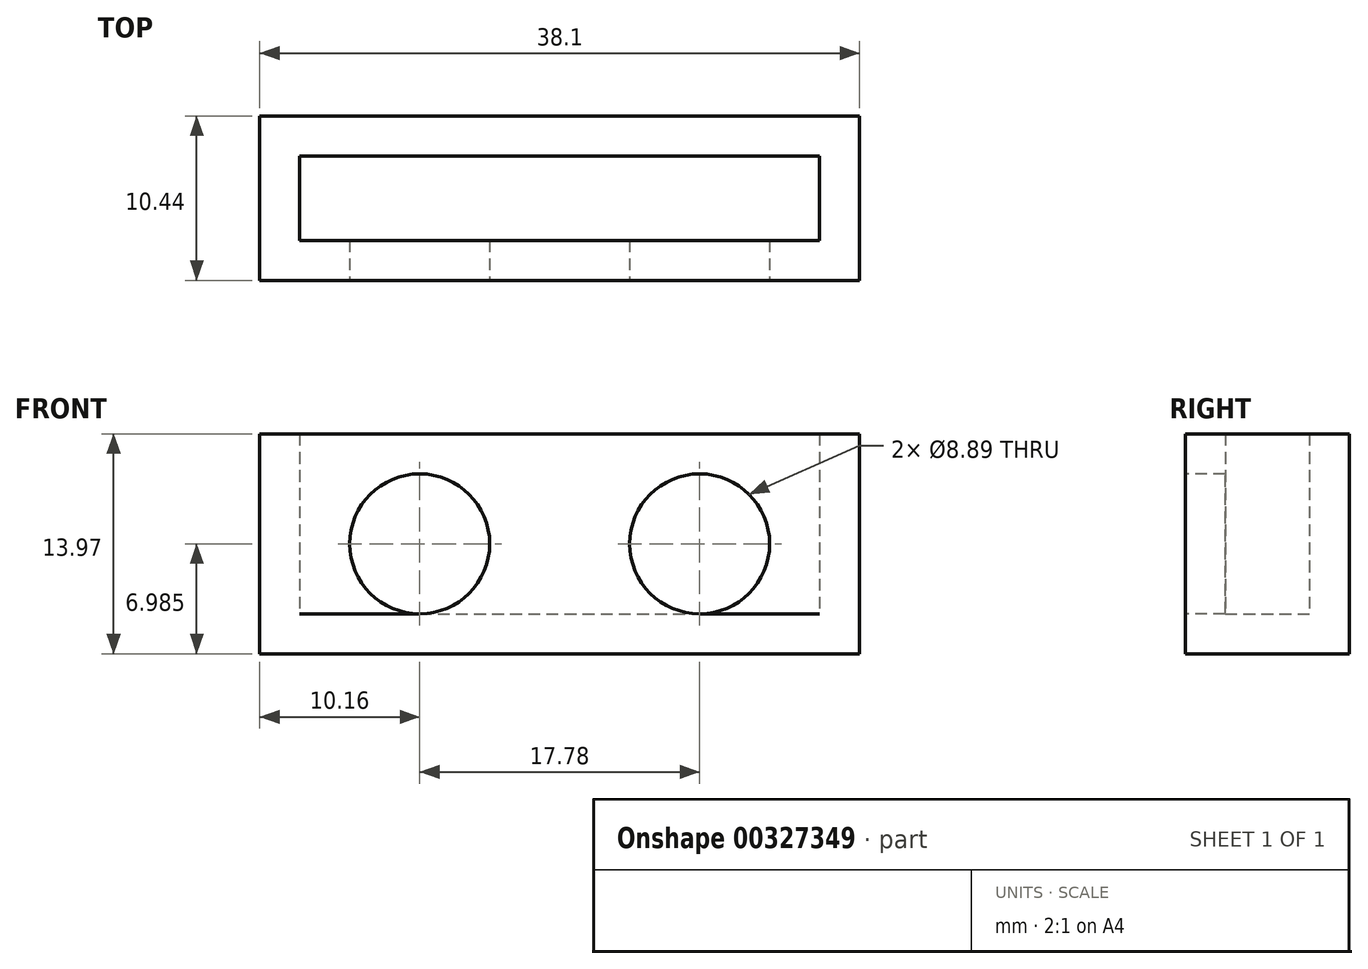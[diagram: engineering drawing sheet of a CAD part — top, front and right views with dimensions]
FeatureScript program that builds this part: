
annotation { "Feature Type Name" : "Feature", "Feature Type Description" : "" }
export const myFeature = defineFeature(function(context is Context, id is Id, definition is map)
    precondition{}
    {
        {
            var Q0;
            Q0=qCreatedBy(makeId("Top.planeOp"),FACE);
            var sketch = newSketch(context, id + "F0", { "sketchPlane" : qUnion([Q0])});
            skLineSegment(sketch, "E0.bottom", {"start": v(-19.05, -5.22) * mm, "end": v(19.05, -5.22) * mm});
            skLineSegment(sketch, "E0.top", {"start": v(-19.05, 5.22) * mm, "end": v(19.05, 5.22) * mm});
            skLineSegment(sketch, "E0.left", {"start": v(-19.05, -5.22) * mm, "end": v(-19.05, 5.22) * mm});
            skLineSegment(sketch, "E0.right", {"start": v(19.05, -5.22) * mm, "end": v(19.05, 5.22) * mm});
            skPoint(sketch, "E0.middle", {"position": v(0, 0) * mm});
            skSolve(sketch);
        }
        {
            var Q0;
            Q0 = qSketchRegion(id + "F0", true);
            extrude(context, id + "F1", {"entities" : qUnion([Q0]), "depth" : 13.97 * mm});
        }
        {
            var Q0;
            Q0=makeQuery(id+"F1.opExtrude","CAP_FACE",FACE,{"disambiguationData":[OSD([sQuery(id+"F0.wireOp",EDGE,"E0.bottom"),sQuery(id+"F0.wireOp",EDGE,"E0.top"),sQuery(id+"F0.wireOp",EDGE,"E0.left"),sQuery(id+"F0.wireOp",EDGE,"E0.right")])],"isStart":false});
            shell(context, id + "F2", {"entities" : qUnion([Q0]), "thickness" : 2.54 * mm});
        }
        {
            var Q0;
            Q0=makeQuery(id+"F1.opExtrude","SWEPT_FACE",FACE,{"disambiguationData":[OSD([sQuery(id+"F0.wireOp",EDGE,"E0.bottom")])]});
            var sketch = newSketch(context, id + "F3", { "sketchPlane" : qUnion([Q0])});
            skPoint(sketch, "E1.centerSnap0", {"position": v(-19.05, 6.99) * mm});
            skCircle(sketch, "E2", {"center": v(8.89, 6.99) * mm, "radius": 5.08 * mm});
            skPoint(sketch, "E2.centerSnap0", {"position": v(19.05, 6.99) * mm});
            skCircle(sketch, "E3", {"center": v(-8.89, 6.99) * mm, "radius": 5.08 * mm});
            skSolve(sketch);
        }
        {
            var Q0;
            Q0=sQuery(id+"F3.wireOp",VERTEX,"E3.center");
            var Q1;
            Q1=sQuery(id+"F3.wireOp",VERTEX,"E2.center");
            var Q2;
            Q2=makeQuery(id+"F1.opExtrude","SWEPT_BODY",BODY,{"disambiguationData":[OSD([sQuery(id+"F0.wireOp",EDGE,"E0.bottom"),sQuery(id+"F0.wireOp",EDGE,"E0.top"),sQuery(id+"F0.wireOp",EDGE,"E0.left"),sQuery(id+"F0.wireOp",EDGE,"E0.right")])]});
            hole(context, id + "F4", {"style" : HoleStyle.SIMPLE, "endStyle" : HoleEndStyle.BLIND, "holeDiameter" : 8.9 * mm, "holeDepth" : 2.54 * mm, "tappedDepth" : 12.7 * mm, "tapClearance" : 3, "locations" : qUnion([Q0, Q1]), "scope" : qUnion([Q2])});
        }
    });
